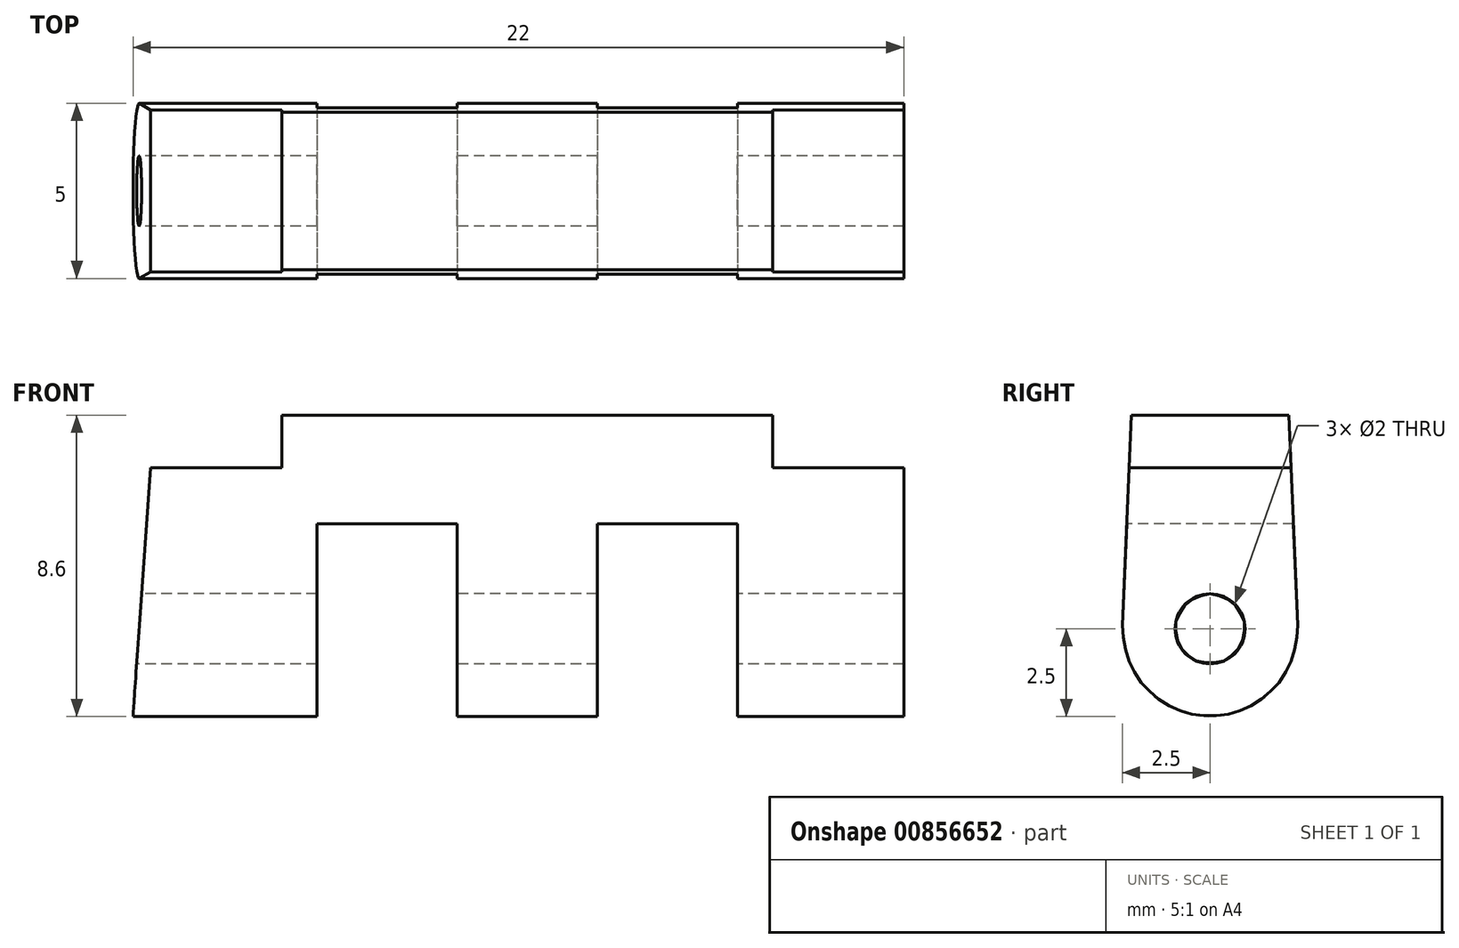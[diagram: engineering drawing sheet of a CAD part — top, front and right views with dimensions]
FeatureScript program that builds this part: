
annotation { "Feature Type Name" : "Feature", "Feature Type Description" : "" }
export const myFeature = defineFeature(function(context is Context, id is Id, definition is map)
    precondition{}
    {
        {
            var Q0;
            Q0=qCreatedBy(makeId("Right.planeOp"),FACE);
            var sketch = newSketch(context, id + "F0", { "sketchPlane" : qUnion([Q0])});
            skCircle(sketch, "E0", {"center": v(0, 0) * mm, "radius": 1 * mm});
            skArc(sketch, "E1", {"start": v(-2.5, 0.1) * mm, "mid": v(0, -2.5) * mm, "end": v(2.5, 0.1) * mm});
            skLineSegment(sketch, "E2", {"start": v(-2.25, 6.1) * mm, "end": v(2.25, 6.1) * mm});
            skLineSegment(sketch, "E3", {"start": v(-2.25, 6.1) * mm, "end": v(-2.5, 0.1) * mm});
            skLineSegment(sketch, "E4", {"start": v(2.25, 6.1) * mm, "end": v(2.5, 0.1) * mm});
            skSolve(sketch);
        }
        {
            var Q0;
            Q0=makeQuery(id+"F0.imprint","IMPRINT",FACE,{"disambiguationData":[TD([[makeQuery(id+"F0.imprint","IMPRINT",EDGE,{"derivedFrom":sQuery(id+"F0.wireOp",EDGE,"E0")}),-1.0]])]});
            extrude(context, id + "F1", {"entities" : qUnion([Q0]), "depth" : 22.5 * mm, "offsetDistance" : 25 * mm});
        }
        {
            var Q0;
            Q0=qCreatedBy(makeId("Front.planeOp"),FACE);
            var sketch = newSketch(context, id + "F2", { "sketchPlane" : qUnion([Q0])});
            skLineSegment(sketch, "E5.0.0", {"start": v(0, 0.1) * mm, "end": v(0, 6.1) * mm});
            skLineSegment(sketch, "E5.0.1", {"start": v(4.25, 6.1) * mm, "end": v(18.25, 6.1) * mm});
            skLineSegment(sketch, "E5.0.2", {"start": v(22.5, 6.1) * mm, "end": v(22.5, 0.1) * mm});
            skLineSegment(sketch, "E6", {"start": v(18.25, 4.6) * mm, "end": v(18.25, 6.1) * mm});
            skLineSegment(sketch, "E7", {"start": v(18.25, 6.1) * mm, "end": v(4.25, 6.1) * mm});
            skLineSegment(sketch, "E8", {"start": v(4.25, 6.1) * mm, "end": v(4.25, 4.6) * mm});
            skLineSegment(sketch, "E9", {"start": v(4.25, 4.6) * mm, "end": v(0.5, 4.6) * mm});
            skLineSegment(sketch, "E10", {"start": v(0.5, 4.6) * mm, "end": v(0, -2.5) * mm});
            skLineSegment(sketch, "E11", {"start": v(22, -2.5) * mm, "end": v(0, -2.5) * mm});
            skLineSegment(sketch, "E12", {"start": v(22, -2.5) * mm, "end": v(22, 4.6) * mm});
            skLineSegment(sketch, "E13", {"start": v(18.25, 4.6) * mm, "end": v(22, 4.6) * mm});
            skPoint(sketch, "E14.orphan", {"position": v(22, 8.45) * mm});
            skLineSegment(sketch, "E15.bottom", {"start": v(5.25, 3) * mm, "end": v(9.25, 3) * mm});
            skLineSegment(sketch, "E15.left", {"start": v(5.25, 3) * mm, "end": v(5.25, -3.5) * mm});
            skLineSegment(sketch, "E15.right", {"start": v(9.25, 3) * mm, "end": v(9.25, -3.5) * mm});
            skLineSegment(sketch, "E16.bottom", {"start": v(13.25, 3) * mm, "end": v(17.25, 3) * mm});
            skLineSegment(sketch, "E16.left", {"start": v(13.25, 3) * mm, "end": v(13.25, -4.62) * mm});
            skLineSegment(sketch, "E16.right", {"start": v(17.25, 3) * mm, "end": v(17.25, -4.62) * mm});
            skLineSegment(sketch, "E17", {"start": v(17.25, -4.62) * mm, "end": v(21.35, -4.62) * mm});
            skLineSegment(sketch, "E18", {"start": v(21.35, -4.62) * mm, "end": v(22, -2.5) * mm});
            skLineSegment(sketch, "E19", {"start": v(13.25, -4.62) * mm, "end": v(9.25, -3.5) * mm});
            skLineSegment(sketch, "E20", {"start": v(5.25, -3.5) * mm, "end": v(0, -2.5) * mm});
            skSolve(sketch);
        }
        {
            var Q0;
            Q0 = qSketchRegion(id + "F2", true);
            extrude(context, id + "F3", {"entities" : qUnion([Q0]), "operationType" : NewBodyOperationType.INTERSECT, "endBound" : BoundingType.SYMMETRIC, "depth" : 25 * mm, "offsetDistance" : 25 * mm});
        }
        {
            var Q0;
            Q0=qCreatedBy(makeId("Front.planeOp"),FACE);
            var sketch = newSketch(context, id + "F4", { "sketchPlane" : qUnion([Q0])});
            skLineSegment(sketch, "E21.bottom", {"start": v(5.25, 3) * mm, "end": v(9.25, 3) * mm});
            skLineSegment(sketch, "E21.left", {"start": v(5.25, 3) * mm, "end": v(5.25, -7) * mm});
            skLineSegment(sketch, "E21.right", {"start": v(9.25, 3) * mm, "end": v(9.25, -5) * mm});
            skLineSegment(sketch, "E22.bottom", {"start": v(13.25, 3) * mm, "end": v(17.25, 3) * mm});
            skLineSegment(sketch, "E22.left", {"start": v(13.25, 3) * mm, "end": v(13.25, -5) * mm});
            skLineSegment(sketch, "E22.right", {"start": v(17.25, 3) * mm, "end": v(17.25, -7) * mm});
            skLineSegment(sketch, "E23", {"start": v(22.5, -2.5) * mm, "end": v(0, -2.5) * mm});
            skLineSegment(sketch, "E24.0.0", {"start": v(0.18, 0.1) * mm, "end": v(22, 0.1) * mm});
            skLineSegment(sketch, "E24.0.1", {"start": v(22, 0.1) * mm, "end": v(22, 4.6) * mm});
            skLineSegment(sketch, "E24.0.2", {"start": v(22, 4.6) * mm, "end": v(18.25, 4.6) * mm});
            skLineSegment(sketch, "E24.0.3", {"start": v(18.25, 4.6) * mm, "end": v(18.25, 6.1) * mm});
            skLineSegment(sketch, "E24.0.4", {"start": v(18.25, 6.1) * mm, "end": v(4.25, 6.1) * mm});
            skLineSegment(sketch, "E24.0.5", {"start": v(4.25, 6.1) * mm, "end": v(4.25, 4.6) * mm});
            skLineSegment(sketch, "E24.0.6", {"start": v(4.25, 4.6) * mm, "end": v(0.5, 4.6) * mm});
            skLineSegment(sketch, "E24.0.7", {"start": v(0.5, 4.6) * mm, "end": v(0.18, 0.1) * mm});
            skLineSegment(sketch, "E25", {"start": v(9.25, -5) * mm, "end": v(13.25, -5) * mm});
            skLineSegment(sketch, "E26", {"start": v(5.25, -7) * mm, "end": v(17.25, -7) * mm});
            skPoint(sketch, "E27.orphan", {"position": v(5.25, -7) * mm});
            skPoint(sketch, "E28.orphan", {"position": v(5.25, -5) * mm});
            skPoint(sketch, "E29.orphan", {"position": v(17.25, -5) * mm});
            skSolve(sketch);
        }
        {
            var Q0;
            {var subQ0=sQuery(id+"F4.wireOp",EDGE,"E21.bottom");Q0=makeQuery(id+"F4.imprint","IMPRINT",FACE,{"disambiguationData":[TD([[makeQuery(id+"F4.imprint","IMPRINT",EDGE,{"derivedFrom":subQ0}),-1.0]])]});}
            var Q1;
            {var subQ0=sQuery(id+"F4.wireOp",EDGE,"E25");Q1=makeQuery(id+"F4.imprint","IMPRINT",FACE,{"disambiguationData":[TD([[makeQuery(id+"F4.imprint","IMPRINT",EDGE,{"derivedFrom":subQ0}),-1.0]])]});}
            var Q2;
            {var subQ0=sQuery(id+"F4.wireOp",EDGE,"E23");var subQ1=sQuery(id+"F4.wireOp",EDGE,"E21.left");var subQ2=makeQuery(id+"F4.imprint","INTERSECT",VERTEX,{"derivedFrom":[subQ1,subQ0]});Q2=makeQuery(id+"F4.imprint","IMPRINT",FACE,{"disambiguationData":[TD([[makeQuery(id+"F4.imprint","IMPRINT",EDGE,{"disambiguationData":[TD([[subQ2,1.0]])],"derivedFrom":subQ1}),1.0]])]});}
            var Q3;
            {var subQ0=sQuery(id+"F4.wireOp",EDGE,"E22.bottom");Q3=makeQuery(id+"F4.imprint","IMPRINT",FACE,{"disambiguationData":[TD([[makeQuery(id+"F4.imprint","IMPRINT",EDGE,{"derivedFrom":subQ0}),-1.0]])]});}
            var Q4;
            {var subQ0=sQuery(id+"F4.wireOp",EDGE,"E24.0.0");var subQ1=sQuery(id+"F4.wireOp",EDGE,"E22.left");var subQ2=makeQuery(id+"F4.imprint","INTERSECT",VERTEX,{"derivedFrom":[subQ1,subQ0]});Q4=makeQuery(id+"F4.imprint","IMPRINT",FACE,{"disambiguationData":[TD([[makeQuery(id+"F4.imprint","IMPRINT",EDGE,{"disambiguationData":[TD([[subQ2,-1.0]])],"derivedFrom":subQ1}),1.0]])]});}
            var Q5;
            Q5=sQuery(id+"F4.wireOp",EDGE,"E21.left");
            var Q6;
            Q6=sQuery(id+"F4.wireOp",EDGE,"E21.bottom");
            var Q7;
            Q7=sQuery(id+"F4.wireOp",EDGE,"E21.right");
            var Q8;
            Q8=sQuery(id+"F4.wireOp",EDGE,"E25");
            var Q9;
            Q9=sQuery(id+"F4.wireOp",EDGE,"E22.left");
            var Q10;
            Q10=sQuery(id+"F4.wireOp",EDGE,"E22.bottom");
            var Q11;
            Q11=sQuery(id+"F4.wireOp",EDGE,"E22.right");
            var Q12;
            Q12=sQuery(id+"F4.wireOp",EDGE,"E26");
            extrude(context, id + "F5", {"entities" : qUnion([Q0, Q1, Q2, Q3, Q4]), "operationType" : NewBodyOperationType.REMOVE, "surfaceEntities" : qUnion([Q5, Q6, Q7, Q8, Q9, Q10, Q11, Q12]), "endBound" : BoundingType.SYMMETRIC, "oppositeDirection" : true, "depth" : 25 * mm, "offsetDistance" : 25 * mm});
        }
    });
